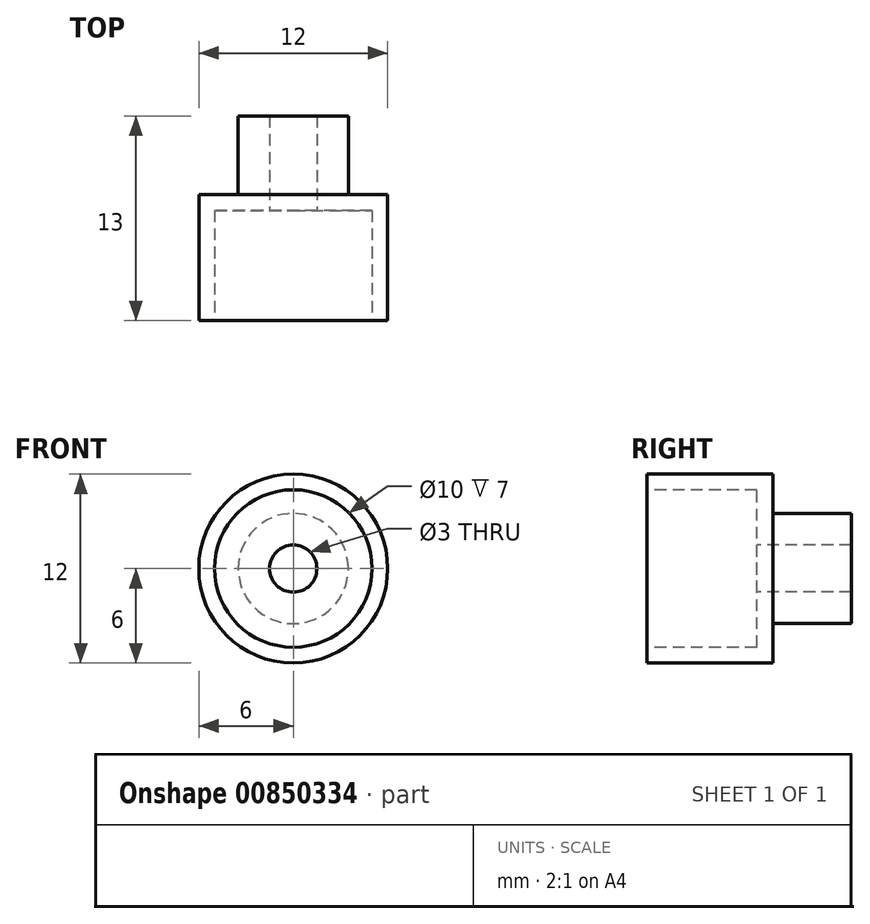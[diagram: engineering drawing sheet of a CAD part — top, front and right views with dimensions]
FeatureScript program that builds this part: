
annotation { "Feature Type Name" : "Feature", "Feature Type Description" : "" }
export const myFeature = defineFeature(function(context is Context, id is Id, definition is map)
    precondition{}
    {
        {
            var Q0;
            Q0=qCreatedBy(makeId("Front.planeOp"),FACE);
            var sketch = newSketch(context, id + "F0", { "sketchPlane" : qUnion([Q0])});
            skCircle(sketch, "E0", {"center": v(0, 0) * mm, "radius": 5 * mm});
            skCircle(sketch, "E1", {"center": v(0, 0) * mm, "radius": 6 * mm});
            skSolve(sketch);
        }
        {
            var Q0;
            Q0=makeQuery(id+"F0.imprint","IMPRINT",FACE,{"disambiguationData":[TD([[makeQuery(id+"F0.imprint","IMPRINT",EDGE,{"derivedFrom":sQuery(id+"F0.wireOp",EDGE,"E0")}),1.0]])]});
            var Q1;
            Q1=makeQuery(id+"F0.imprint","IMPRINT",FACE,{"disambiguationData":[TD([[makeQuery(id+"F0.imprint","IMPRINT",EDGE,{"derivedFrom":sQuery(id+"F0.wireOp",EDGE,"E0")}),-1.0]])]});
            extrude(context, id + "F1", {"entities" : qUnion([Q0, Q1]), "oppositeDirection" : true, "depth" : 8 * mm, "offsetDistance" : 25 * mm});
        }
        {
            var Q0;
            Q0=qCreatedBy(makeId("Front.planeOp"),FACE);
            cPlane(context, id + "F2", {"entities" : qUnion([Q0]), "cplaneType" : CPlaneType.OFFSET, "offset" : 8 * mm, "oppositeDirection" : true, "width" : 150 * mm, "height" : 150 * mm});
        }
        {
            var Q0;
            Q0=qCreatedBy(id+"F2.planeOp",FACE);
            var sketch = newSketch(context, id + "F3", { "sketchPlane" : qUnion([Q0])});
            skCircle(sketch, "E2", {"center": v(0, 0) * mm, "radius": 3.5 * mm});
            skCircle(sketch, "E3", {"center": v(0, 0) * mm, "radius": 1.5 * mm});
            skSolve(sketch);
        }
        {
            var Q0;
            Q0=makeQuery(id+"F3.imprint","IMPRINT",FACE,{"disambiguationData":[TD([[makeQuery(id+"F3.imprint","IMPRINT",EDGE,{"derivedFrom":sQuery(id+"F3.wireOp",EDGE,"E2")}),1.0]])]});
            var Q1;
            Q1=makeQuery(id+"F3.imprint","IMPRINT",FACE,{"disambiguationData":[TD([[makeQuery(id+"F3.imprint","IMPRINT",EDGE,{"derivedFrom":sQuery(id+"F3.wireOp",EDGE,"E3")}),1.0]])]});
            extrude(context, id + "F4", {"entities" : qUnion([Q0, Q1]), "operationType" : NewBodyOperationType.ADD, "oppositeDirection" : true, "depth" : 5 * mm, "offsetDistance" : 25 * mm});
        }
        {
            var Q0;
            Q0=qCreatedBy(makeId("Front.planeOp"),FACE);
            var sketch = newSketch(context, id + "F5", { "sketchPlane" : qUnion([Q0])});
            skCircle(sketch, "E4", {"center": v(0, 0) * mm, "radius": 5 * mm});
            skSolve(sketch);
        }
        {
            var Q0;
            Q0 = qSketchRegion(id + "F5", true);
            extrude(context, id + "F6", {"entities" : qUnion([Q0]), "operationType" : NewBodyOperationType.REMOVE, "oppositeDirection" : true, "depth" : 7 * mm, "offsetDistance" : 25 * mm});
        }
        {
            var Q0;
            Q0=qCreatedBy(makeId("Front.planeOp"),FACE);
            var sketch = newSketch(context, id + "F7", { "sketchPlane" : qUnion([Q0])});
            skCircle(sketch, "E5", {"center": v(0, 0) * mm, "radius": 1.5 * mm});
            skSolve(sketch);
        }
        {
            var Q0;
            Q0 = qSketchRegion(id + "F7", true);
            extrude(context, id + "F8", {"entities" : qUnion([Q0]), "operationType" : NewBodyOperationType.REMOVE, "oppositeDirection" : true, "depth" : 25 * mm, "offsetDistance" : 25 * mm});
        }
    });
